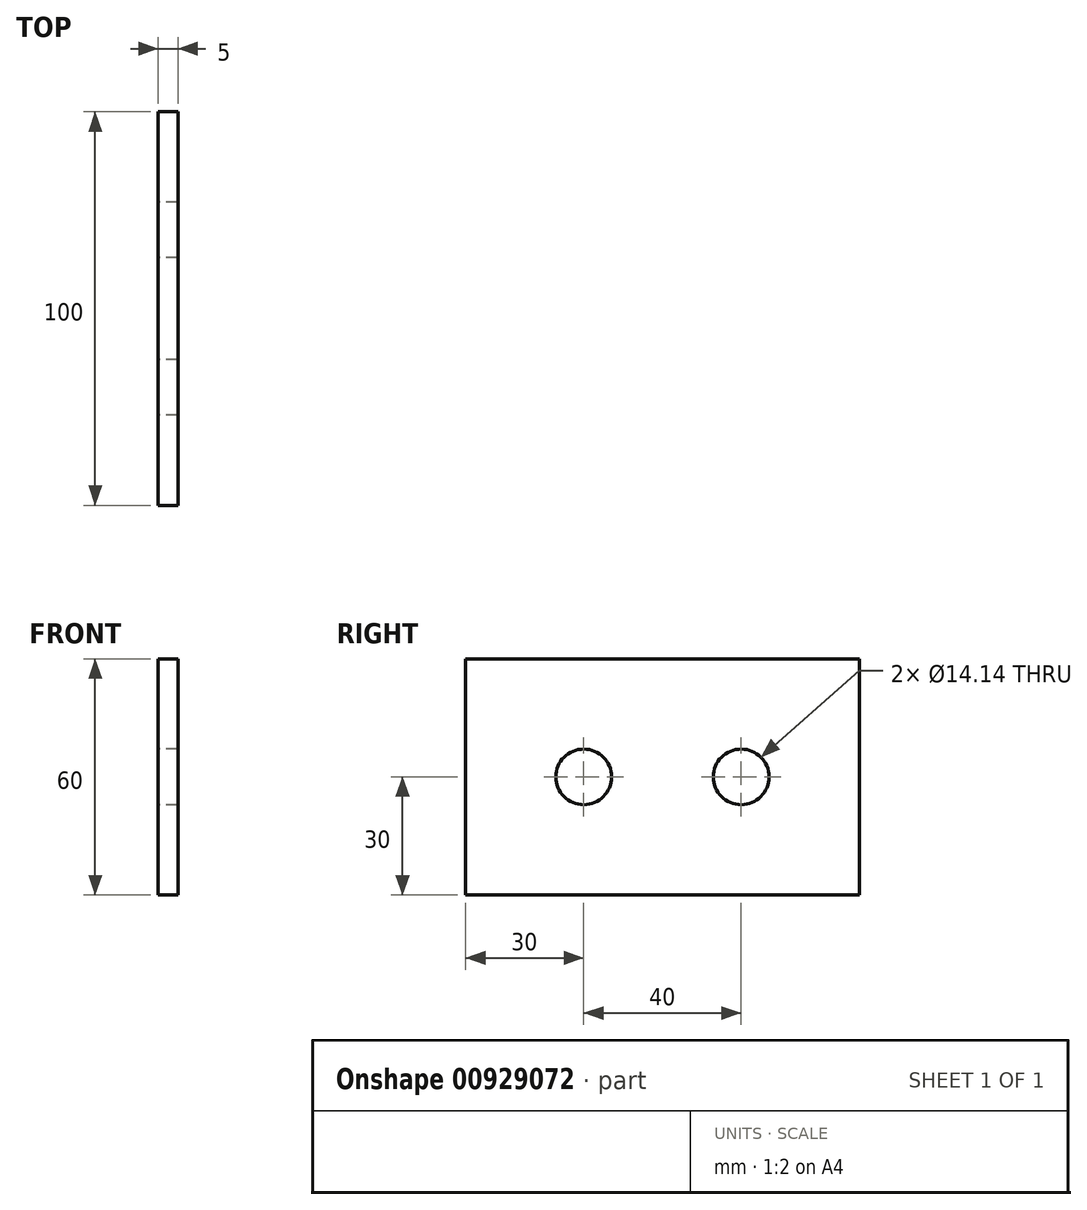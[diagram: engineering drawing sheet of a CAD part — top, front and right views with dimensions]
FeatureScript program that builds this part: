
annotation { "Feature Type Name" : "Feature", "Feature Type Description" : "" }
export const myFeature = defineFeature(function(context is Context, id is Id, definition is map)
    precondition{}
    {
        {
            var Q0;
            Q0=qCreatedBy(makeId("Right.planeOp"),FACE);
            var sketch = newSketch(context, id + "F0", { "sketchPlane" : qUnion([Q0])});
            skCircle(sketch, "E0", {"center": v(0, 0) * mm, "radius": 7.07 * mm});
            skCircle(sketch, "E1", {"center": v(40, 0) * mm, "radius": 7.07 * mm});
            skLineSegment(sketch, "E2.bottom", {"start": v(-30, -30) * mm, "end": v(70, -30) * mm});
            skLineSegment(sketch, "E2.top", {"start": v(-30, 30) * mm, "end": v(70, 30) * mm});
            skLineSegment(sketch, "E2.left", {"start": v(-30, -30) * mm, "end": v(-30, 30) * mm});
            skLineSegment(sketch, "E2.right", {"start": v(70, -30) * mm, "end": v(70, 30) * mm});
            skSolve(sketch);
        }
        {
            var Q0;
            Q0 = qSketchRegion(id + "F0", true);
            extrude(context, id + "F1", {"entities" : qUnion([Q0]), "depth" : 5 * mm, "offsetDistance" : 25 * mm});
        }
    });
